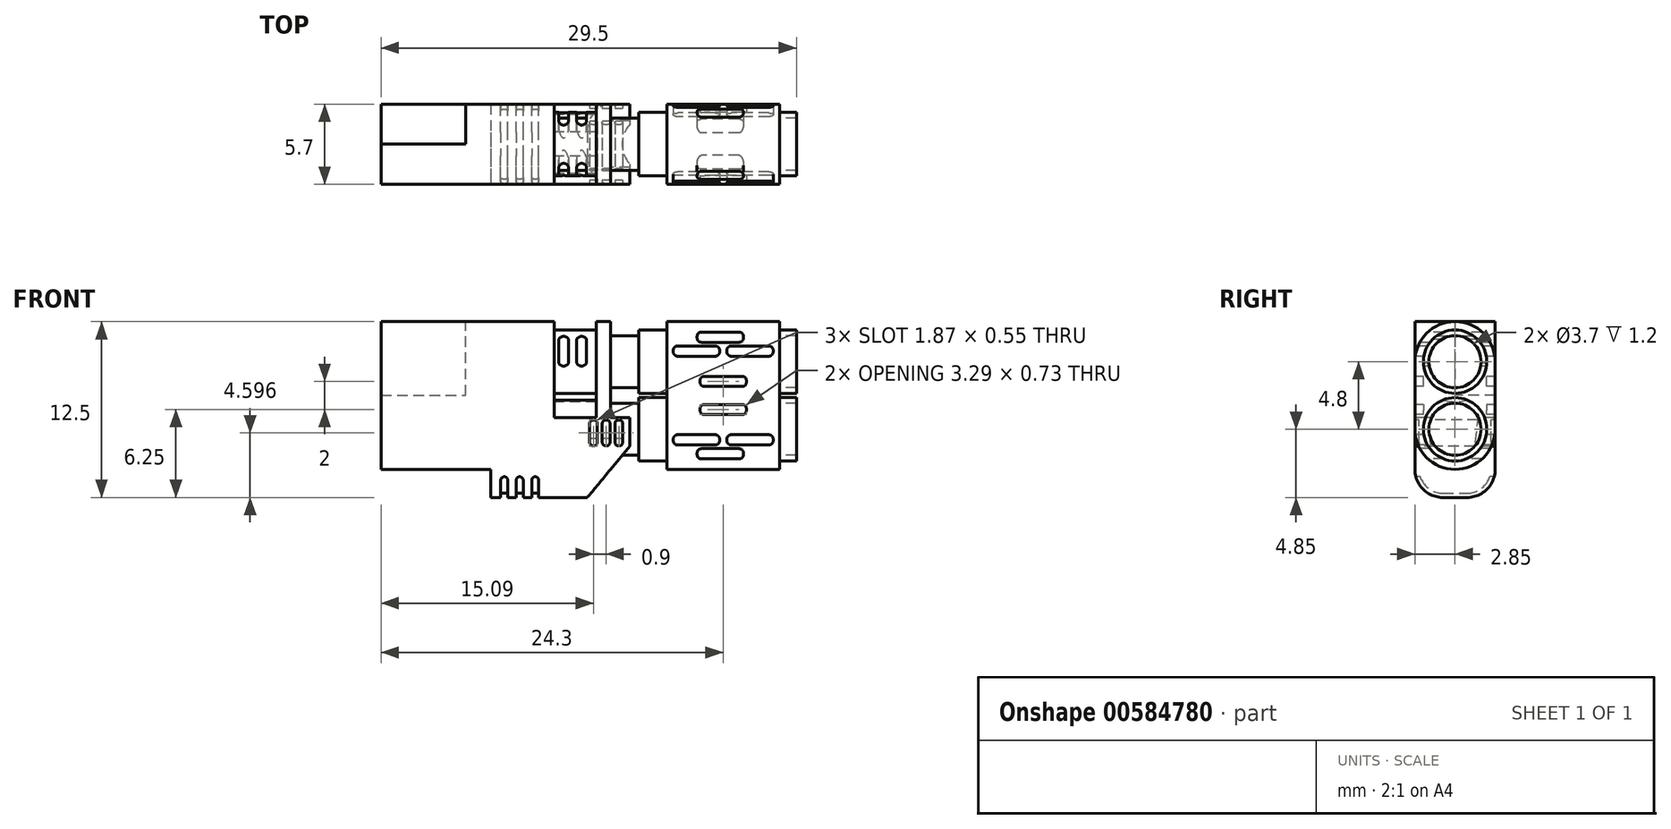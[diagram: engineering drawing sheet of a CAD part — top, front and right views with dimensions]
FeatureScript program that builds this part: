
annotation { "Feature Type Name" : "Feature", "Feature Type Description" : "" }
export const myFeature = defineFeature(function(context is Context, id is Id, definition is map)
    precondition{}
    {
        {
            var Q0;
            Q0=qCreatedBy(makeId("Front.planeOp"),FACE);
            var sketch = newSketch(context, id + "F0", { "sketchPlane" : qUnion([Q0])});
            skLineSegment(sketch, "E0.bottom", {"start": v(-20.5, 0) * mm, "end": v(-8.2, 0) * mm});
            skLineSegment(sketch, "E0.top", {"start": v(-20.5, 10.5) * mm, "end": v(-8.2, 10.5) * mm});
            skLineSegment(sketch, "E0.left", {"start": v(-20.5, 0) * mm, "end": v(-20.5, 10.5) * mm});
            skLineSegment(sketch, "E0.right", {"start": v(-8.2, 0) * mm, "end": v(-8.2, 10.5) * mm});
            skLineSegment(sketch, "E1", {"start": v(-20.5, 5.25) * mm, "end": v(-14.5, 5.25) * mm});
            skPoint(sketch, "E1.endSnap0", {"position": v(-20.5, 5.25) * mm});
            skLineSegment(sketch, "E2", {"start": v(-14.5, 5.25) * mm, "end": v(-14.5, 10.5) * mm});
            skLineSegment(sketch, "E3", {"start": v(-12.7, 2.94) * mm, "end": v(-12.7, 0) * mm, "construction": true});
            skSolve(sketch);
        }
        {
            var Q0;
            {var subQ1=sQuery(id+"F0.wireOp",EDGE,"E0.bottom");Q0=makeQuery(id+"F0.imprint","IMPRINT",FACE,{"disambiguationData":[TD([[makeQuery(id+"F0.imprint","IMPRINT",EDGE,{"derivedFrom":subQ1}),1.0]])]});}
            extrude(context, id + "F1", {"entities" : qUnion([Q0]), "oppositeDirection" : true, "depth" : 5.7 * mm, "offsetDistance" : 25 * mm});
        }
        {
            var Q0;
            {var subQ4=sQuery(id+"F0.wireOp",EDGE,"E1");Q0=makeQuery(id+"F0.imprint","IMPRINT",FACE,{"disambiguationData":[TD([[makeQuery(id+"F0.imprint","IMPRINT",EDGE,{"derivedFrom":subQ4}),1.0]])]});}
            extrude(context, id + "F2", {"entities" : qUnion([Q0]), "operationType" : NewBodyOperationType.ADD, "oppositeDirection" : true, "depth" : 2.87 * mm, "offsetDistance" : 25 * mm});
        }
        {
            var Q0;
            Q0=makeQuery(id+"F1.opExtrude","SWEPT_FACE",FACE,{"disambiguationData":[OSD([sQuery(id+"F0.wireOp",EDGE,"E0.right")])]});
            var sketch = newSketch(context, id + "F3", { "sketchPlane" : qUnion([Q0])});
            skArc(sketch, "E4", {"start": v(5.7, 7.65) * mm, "mid": v(2.85, 10.5) * mm, "end": v(0, 7.65) * mm});
            skArc(sketch, "E5", {"start": v(0, 2.85) * mm, "mid": v(2.85, 0) * mm, "end": v(5.7, 2.85) * mm});
            skPoint(sketch, "E5.centerSnap0", {"position": v(2.85, 10.5) * mm});
            skLineSegment(sketch, "E6", {"start": v(2.85, 10.5) * mm, "end": v(2.85, 0) * mm, "construction": true});
            skPoint(sketch, "E7", {"position": v(0, 7.65) * mm});
            skPoint(sketch, "E8", {"position": v(5.7, 7.65) * mm});
            skPoint(sketch, "E9", {"position": v(5.7, 2.85) * mm});
            skPoint(sketch, "E10", {"position": v(0, 2.85) * mm});
            skLineSegment(sketch, "E11", {"start": v(0, 7.65) * mm, "end": v(0, 2.85) * mm});
            skLineSegment(sketch, "E12", {"start": v(5.7, 7.65) * mm, "end": v(5.7, 2.85) * mm});
            skCircle(sketch, "E13", {"center": v(2.85, 7.65) * mm, "radius": 2.25 * mm});
            skCircle(sketch, "E14", {"center": v(2.85, 2.85) * mm, "radius": 2.25 * mm});
            skCircle(sketch, "E15", {"center": v(2.85, 2.85) * mm, "radius": 2.85 * mm});
            skCircle(sketch, "E16", {"center": v(2.85, 7.65) * mm, "radius": 2.85 * mm});
            skCircle(sketch, "E17", {"center": v(2.85, 7.65) * mm, "radius": 1.85 * mm});
            skCircle(sketch, "E18", {"center": v(2.85, 2.85) * mm, "radius": 1.85 * mm});
            skSolve(sketch);
        }
        {
            var Q0;
            Q0=makeQuery(id+"F3.imprint","IMPRINT",FACE,{"disambiguationData":[TD([[makeQuery(id+"F3.imprint","IMPRINT",EDGE,{"derivedFrom":sQuery(id+"F3.wireOp",EDGE,"E17")}),-1.0]])]});
            var Q1;
            Q1=makeQuery(id+"F3.imprint","IMPRINT",FACE,{"disambiguationData":[TD([[makeQuery(id+"F3.imprint","IMPRINT",EDGE,{"derivedFrom":sQuery(id+"F3.wireOp",EDGE,"E17")}),1.0]])]});
            var Q2;
            Q2=makeQuery(id+"F3.imprint","IMPRINT",FACE,{"disambiguationData":[TD([[makeQuery(id+"F3.imprint","IMPRINT",EDGE,{"derivedFrom":sQuery(id+"F3.wireOp",EDGE,"E18")}),-1.0]])]});
            var Q3;
            Q3=makeQuery(id+"F3.imprint","IMPRINT",FACE,{"disambiguationData":[TD([[makeQuery(id+"F3.imprint","IMPRINT",EDGE,{"derivedFrom":sQuery(id+"F3.wireOp",EDGE,"E18")}),1.0]])]});
            var Q4;
            {var subQ0=sQuery(id+"F3.wireOp",EDGE,"E16");var subQ1=sQuery(id+"F3.wireOp",EDGE,"E14");var subQ2=makeQuery(id+"F3.imprint","INTERSECT",VERTEX,{"disambiguationData":[OD(0.0)],"derivedFrom":[subQ1,subQ0]});Q4=makeQuery(id+"F3.imprint","IMPRINT",FACE,{"disambiguationData":[TD([[makeQuery(id+"F3.imprint","IMPRINT",EDGE,{"disambiguationData":[TD([[subQ2,1.0]])],"derivedFrom":subQ1}),1.0]])]});}
            var Q5;
            {var subQ0=sQuery(id+"F3.wireOp",EDGE,"E15");var subQ1=sQuery(id+"F3.wireOp",EDGE,"E13");var subQ2=makeQuery(id+"F3.imprint","INTERSECT",VERTEX,{"disambiguationData":[OD(0.0)],"derivedFrom":[subQ1,subQ0]});Q5=makeQuery(id+"F3.imprint","IMPRINT",FACE,{"disambiguationData":[TD([[makeQuery(id+"F3.imprint","IMPRINT",EDGE,{"disambiguationData":[TD([[subQ2,1.0]])],"derivedFrom":subQ1}),1.0]])]});}
            extrude(context, id + "F4", {"entities" : qUnion([Q0, Q1, Q2, Q3, Q4, Q5]), "operationType" : NewBodyOperationType.ADD, "depth" : 3 * mm, "offsetDistance" : 25 * mm});
        }
        {
            var Q0;
            Q0=makeQuery(id+"F4.opExtrude","CAP_FACE",FACE,{"disambiguationData":[OSD([sQuery(id+"F3.wireOp",EDGE,"E13")])],"isStart":false});
            var sketch = newSketch(context, id + "F5", { "sketchPlane" : qUnion([Q0])});
            skArc(sketch, "E19.0", {"start": v(5.7, 7.65) * mm, "mid": v(2.85, 10.5) * mm, "end": v(0, 7.65) * mm});
            skArc(sketch, "E19.1", {"start": v(0, 2.85) * mm, "mid": v(2.85, 0) * mm, "end": v(5.7, 2.85) * mm});
            skLineSegment(sketch, "E19.2", {"start": v(0, 7.65) * mm, "end": v(0, 2.85) * mm});
            skLineSegment(sketch, "E19.3", {"start": v(5.7, 7.65) * mm, "end": v(5.7, 2.85) * mm});
            skSolve(sketch);
        }
        {
            var Q0;
            Q0 = qSketchRegion(id + "F5", true);
            extrude(context, id + "F6", {"entities" : qUnion([Q0]), "operationType" : NewBodyOperationType.ADD, "depth" : 1 * mm, "offsetDistance" : 25 * mm});
        }
        {
            var Q0;
            Q0=makeQuery(id+"F6.opExtrude","CAP_FACE",FACE,{"disambiguationData":[OSD([sQuery(id+"F5.wireOp",EDGE,"E19.0"),sQuery(id+"F5.wireOp",EDGE,"E19.1"),sQuery(id+"F5.wireOp",EDGE,"E19.2"),sQuery(id+"F5.wireOp",EDGE,"E19.3")])],"isStart":false});
            var sketch = newSketch(context, id + "F7", { "sketchPlane" : qUnion([Q0])});
            skCircle(sketch, "E20.0", {"center": v(2.85, 7.65) * mm, "radius": 1.85 * mm});
            skCircle(sketch, "E20.1", {"center": v(2.85, 2.85) * mm, "radius": 1.85 * mm});
            skSolve(sketch);
        }
        {
            var Q0;
            Q0=makeQuery(id+"F7.imprint","IMPRINT",FACE,{"disambiguationData":[TD([[makeQuery(id+"F7.imprint","IMPRINT",EDGE,{"derivedFrom":sQuery(id+"F7.wireOp",EDGE,"E20.0")}),1.0]])]});
            var Q1;
            Q1=makeQuery(id+"F7.imprint","IMPRINT",FACE,{"disambiguationData":[TD([[makeQuery(id+"F7.imprint","IMPRINT",EDGE,{"derivedFrom":sQuery(id+"F7.wireOp",EDGE,"E20.1")}),1.0]])]});
            extrude(context, id + "F8", {"entities" : qUnion([Q0, Q1]), "operationType" : NewBodyOperationType.ADD, "depth" : 2 * mm, "offsetDistance" : 25 * mm});
        }
        {
            var Q0;
            Q0=makeQuery(id+"F8.opExtrude","CAP_FACE",FACE,{"disambiguationData":[OSD([sQuery(id+"F7.wireOp",EDGE,"E20.0")])],"isStart":false});
            var sketch = newSketch(context, id + "F9", { "sketchPlane" : qUnion([Q0])});
            skCircle(sketch, "E21.0", {"center": v(2.85, 7.65) * mm, "radius": 2.25 * mm});
            skCircle(sketch, "E21.1", {"center": v(2.85, 2.85) * mm, "radius": 2.25 * mm});
            skSolve(sketch);
        }
        {
            var Q0;
            Q0=makeQuery(id+"F9.imprint","IMPRINT",FACE,{"disambiguationData":[TD([[makeQuery(id+"F9.imprint","IMPRINT",EDGE,{"derivedFrom":sQuery(id+"F9.wireOp",EDGE,"E21.0")}),1.0]])]});
            var Q1;
            Q1=makeQuery(id+"F9.imprint","IMPRINT",FACE,{"disambiguationData":[TD([[makeQuery(id+"F9.imprint","IMPRINT",EDGE,{"derivedFrom":makeQuery(id+"F8.opExtrude","CAP_EDGE",EDGE,{"disambiguationData":[OSD([sQuery(id+"F7.wireOp",EDGE,"E20.0")])],"isStart":false})}),1.0]])]});
            var Q2;
            Q2=makeQuery(id+"F9.imprint","IMPRINT",FACE,{"disambiguationData":[TD([[makeQuery(id+"F9.imprint","IMPRINT",EDGE,{"derivedFrom":sQuery(id+"F9.wireOp",EDGE,"E21.1")}),1.0]])]});
            extrude(context, id + "F10", {"entities" : qUnion([Q0, Q1, Q2]), "operationType" : NewBodyOperationType.ADD, "depth" : 2 * mm, "offsetDistance" : 25 * mm});
        }
        {
            var Q0;
            Q0=makeQuery(id+"F10.opExtrude","CAP_FACE",FACE,{"disambiguationData":[OSD([sQuery(id+"F9.wireOp",EDGE,"E21.0")])],"isStart":false});
            var sketch = newSketch(context, id + "F11", { "sketchPlane" : qUnion([Q0])});
            skLineSegment(sketch, "E22.0.0", {"start": v(0, 7.65) * mm, "end": v(0, 2.85) * mm});
            skArc(sketch, "E22.0.1", {"start": v(0, 2.85) * mm, "mid": v(2.85, 0) * mm, "end": v(5.7, 2.85) * mm});
            skLineSegment(sketch, "E22.0.2", {"start": v(5.7, 2.85) * mm, "end": v(5.7, 7.65) * mm});
            skArc(sketch, "E22.0.3", {"start": v(5.7, 7.65) * mm, "mid": v(2.85, 10.5) * mm, "end": v(0, 7.65) * mm});
            skSolve(sketch);
        }
        {
            var Q0;
            Q0=makeQuery(id+"F11.imprint","IMPRINT",FACE,{"disambiguationData":[TD([[makeQuery(id+"F11.imprint","IMPRINT",EDGE,{"derivedFrom":makeQuery(id+"F10.opExtrude","CAP_EDGE",EDGE,{"disambiguationData":[OSD([sQuery(id+"F9.wireOp",EDGE,"E21.0")])],"isStart":false})}),1.0]])]});
            var Q1;
            Q1=makeQuery(id+"F11.imprint","IMPRINT",FACE,{"disambiguationData":[TD([[makeQuery(id+"F11.imprint","IMPRINT",EDGE,{"derivedFrom":sQuery(id+"F11.wireOp",EDGE,"E22.0.0")}),1.0]])]});
            extrude(context, id + "F12", {"entities" : qUnion([Q0, Q1]), "operationType" : NewBodyOperationType.ADD, "depth" : 8 * mm, "offsetDistance" : 25 * mm});
        }
        {
            var Q0;
            Q0=makeQuery(id+"F12.opExtrude","CAP_FACE",FACE,{"disambiguationData":[OSD([sQuery(id+"F11.wireOp",EDGE,"E22.0.0"),sQuery(id+"F11.wireOp",EDGE,"E22.0.1"),sQuery(id+"F11.wireOp",EDGE,"E22.0.2"),sQuery(id+"F11.wireOp",EDGE,"E22.0.3")])],"isStart":false});
            var sketch = newSketch(context, id + "F13", { "sketchPlane" : qUnion([Q0])});
            skCircle(sketch, "E23.0", {"center": v(2.85, 7.65) * mm, "radius": 2.25 * mm});
            skCircle(sketch, "E23.1", {"center": v(2.85, 7.65) * mm, "radius": 1.85 * mm});
            skCircle(sketch, "E23.2", {"center": v(2.85, 2.85) * mm, "radius": 2.25 * mm});
            skCircle(sketch, "E23.3", {"center": v(2.85, 2.85) * mm, "radius": 1.85 * mm});
            skSolve(sketch);
        }
        {
            var Q0;
            Q0=makeQuery(id+"F13.imprint","IMPRINT",FACE,{"disambiguationData":[TD([[makeQuery(id+"F13.imprint","IMPRINT",EDGE,{"derivedFrom":sQuery(id+"F13.wireOp",EDGE,"E23.0")}),1.0]])]});
            var Q1;
            Q1=makeQuery(id+"F13.imprint","IMPRINT",FACE,{"disambiguationData":[TD([[makeQuery(id+"F13.imprint","IMPRINT",EDGE,{"derivedFrom":sQuery(id+"F13.wireOp",EDGE,"E23.2")}),1.0]])]});
            extrude(context, id + "F14", {"entities" : qUnion([Q0, Q1]), "operationType" : NewBodyOperationType.ADD, "depth" : 1.2 * mm, "offsetDistance" : 25 * mm});
        }
        {
            var Q0;
            {var subQ1=sQuery(id+"F0.wireOp",EDGE,"E0.bottom");Q0=makeQuery(id+"F0.imprint","IMPRINT",FACE,{"disambiguationData":[TD([[makeQuery(id+"F0.imprint","IMPRINT",EDGE,{"derivedFrom":subQ1}),1.0]])]});}
            var sketch = newSketch(context, id + "F15", { "sketchPlane" : qUnion([Q0])});
            skLineSegment(sketch, "E24", {"start": v(-7.53, 9.45) * mm, "end": v(-7.53, 7.34) * mm});
            skLineSegment(sketch, "E25.bottom", {"start": v(-7.18, 9.23) * mm, "end": v(-7.88, 9.23) * mm});
            skLineSegment(sketch, "E25.top", {"start": v(-7.18, 7.55) * mm, "end": v(-7.88, 7.55) * mm});
            skLineSegment(sketch, "E25.left", {"start": v(-7.18, 9.23) * mm, "end": v(-7.18, 7.55) * mm});
            skLineSegment(sketch, "E25.right", {"start": v(-7.88, 9.23) * mm, "end": v(-7.88, 7.55) * mm});
            skPoint(sketch, "E25.middle", {"position": v(-7.53, 8.4) * mm});
            skArc(sketch, "E26", {"start": v(-7.18, 9.23) * mm, "mid": v(-7.53, 9.45) * mm, "end": v(-7.88, 9.23) * mm});
            skArc(sketch, "E27", {"start": v(-7.88, 7.55) * mm, "mid": v(-7.53, 7.34) * mm, "end": v(-7.18, 7.55) * mm});
            skLineSegment(sketch, "E28", {"start": v(-7.88, 9.23) * mm, "end": v(-5.81, 9.23) * mm, "construction": true});
            skLineSegment(sketch, "E29", {"start": v(-7.53, 8.4) * mm, "end": v(-5.83, 8.4) * mm, "construction": true});
            skLineSegment(sketch, "E30", {"start": v(-6.9, 9.77) * mm, "end": v(-6.9, 7.35) * mm, "construction": true});
            skLineSegment(sketch, "E31.MirrorCS", {"start": v(-6.6, 9.23) * mm, "end": v(-6.6, 7.55) * mm});
            skArc(sketch, "E32.MirrorCS", {"start": v(-6.6, 9.23) * mm, "mid": v(-6.25, 9.45) * mm, "end": v(-5.9, 9.23) * mm});
            skLineSegment(sketch, "E33.MirrorCS", {"start": v(-5.9, 9.23) * mm, "end": v(-5.9, 7.55) * mm});
            skArc(sketch, "E34.MirrorCS", {"start": v(-5.9, 7.55) * mm, "mid": v(-6.25, 7.34) * mm, "end": v(-6.6, 7.55) * mm});
            skSolve(sketch);
        }
        {
            var Q0;
            {var subQ0=sQuery(id+"F15.wireOp",EDGE,"E26");var subQ1=sQuery(id+"F15.wireOp",EDGE,"E24");var subQ2=makeQuery(id+"F15.imprint","INTERSECT",VERTEX,{"derivedFrom":[subQ1,subQ0]});Q0=makeQuery(id+"F15.imprint","IMPRINT",FACE,{"disambiguationData":[TD([[makeQuery(id+"F15.imprint","IMPRINT",EDGE,{"disambiguationData":[TD([[subQ2,-1.0]])],"derivedFrom":subQ1}),-1.0]])]});}
            var Q1;
            {var subQ0=sQuery(id+"F15.wireOp",EDGE,"E26");var subQ1=sQuery(id+"F15.wireOp",EDGE,"E24");var subQ2=makeQuery(id+"F15.imprint","INTERSECT",VERTEX,{"derivedFrom":[subQ1,subQ0]});Q1=makeQuery(id+"F15.imprint","IMPRINT",FACE,{"disambiguationData":[TD([[makeQuery(id+"F15.imprint","IMPRINT",EDGE,{"disambiguationData":[TD([[subQ2,-1.0]])],"derivedFrom":subQ1}),1.0]])]});}
            var Q2;
            {var subQ5=sQuery(id+"F15.wireOp",EDGE,"E25.left");Q2=makeQuery(id+"F15.imprint","IMPRINT",FACE,{"disambiguationData":[TD([[makeQuery(id+"F15.imprint","IMPRINT",EDGE,{"derivedFrom":subQ5}),-1.0]])]});}
            var Q3;
            {var subQ5=sQuery(id+"F15.wireOp",EDGE,"E25.right");Q3=makeQuery(id+"F15.imprint","IMPRINT",FACE,{"disambiguationData":[TD([[makeQuery(id+"F15.imprint","IMPRINT",EDGE,{"derivedFrom":subQ5}),1.0]])]});}
            var Q4;
            {var subQ0=sQuery(id+"F15.wireOp",EDGE,"E27");var subQ1=sQuery(id+"F15.wireOp",EDGE,"E24");var subQ2=makeQuery(id+"F15.imprint","INTERSECT",VERTEX,{"derivedFrom":[subQ1,subQ0]});Q4=makeQuery(id+"F15.imprint","IMPRINT",FACE,{"disambiguationData":[TD([[makeQuery(id+"F15.imprint","IMPRINT",EDGE,{"disambiguationData":[TD([[subQ2,1.0]])],"derivedFrom":subQ1}),-1.0]])]});}
            var Q5;
            {var subQ0=sQuery(id+"F15.wireOp",EDGE,"E27");var subQ1=sQuery(id+"F15.wireOp",EDGE,"E24");var subQ2=makeQuery(id+"F15.imprint","INTERSECT",VERTEX,{"derivedFrom":[subQ1,subQ0]});Q5=makeQuery(id+"F15.imprint","IMPRINT",FACE,{"disambiguationData":[TD([[makeQuery(id+"F15.imprint","IMPRINT",EDGE,{"disambiguationData":[TD([[subQ2,1.0]])],"derivedFrom":subQ1}),1.0]])]});}
            extrude(context, id + "F16", {"entities" : qUnion([Q0, Q1, Q2, Q3, Q4, Q5]), "operationType" : NewBodyOperationType.REMOVE, "oppositeDirection" : true, "depth" : 6 * mm, "offsetDistance" : 25 * mm});
        }
        {
            var Q0;
            Q0=makeQuery(id+"F15.imprint","IMPRINT",FACE,{"disambiguationData":[TD([[makeQuery(id+"F15.imprint","IMPRINT",EDGE,{"derivedFrom":sQuery(id+"F15.wireOp",EDGE,"E31.MirrorCS")}),1.0]])]});
            extrude(context, id + "F17", {"entities" : qUnion([Q0]), "operationType" : NewBodyOperationType.REMOVE, "oppositeDirection" : true, "depth" : 6 * mm, "offsetDistance" : 25 * mm});
        }
        {
            var Q0;
            Q0=makeQuery(id+"F3.imprint","IMPRINT",FACE,{"disambiguationData":[TD([[makeQuery(id+"F3.imprint","IMPRINT",EDGE,{"derivedFrom":sQuery(id+"F3.wireOp",EDGE,"E17")}),1.0]])]});
            extrude(context, id + "F18", {"entities" : qUnion([Q0]), "operationType" : NewBodyOperationType.ADD, "depth" : 5 * mm, "offsetDistance" : 25 * mm});
        }
        {
            var Q0;
            Q0=makeQuery(id+"F12.opExtrude","SWEPT_FACE",FACE,{"disambiguationData":[OSD([sQuery(id+"F11.wireOp",EDGE,"E22.0.0")])]});
            var sketch = newSketch(context, id + "F19", { "sketchPlane" : qUnion([Q0])});
            skLineSegment(sketch, "E35", {"start": v(-0.2, 5.25) * mm, "end": v(7.8, 5.25) * mm, "construction": true});
            skLineSegment(sketch, "E36", {"start": v(3.8, 5.25) * mm, "end": v(3.8, 10.5) * mm, "construction": true});
            skLineSegment(sketch, "E37.bottom", {"start": v(5.14, 5.89) * mm, "end": v(2.46, 5.89) * mm});
            skLineSegment(sketch, "E37.top", {"start": v(5.14, 6.61) * mm, "end": v(2.46, 6.61) * mm});
            skLineSegment(sketch, "E37.left", {"start": v(5.44, 6.19) * mm, "end": v(5.44, 6.31) * mm});
            skLineSegment(sketch, "E37.right", {"start": v(2.16, 6.19) * mm, "end": v(2.16, 6.31) * mm});
            skPoint(sketch, "E37.middle", {"position": v(3.8, 6.25) * mm});
            skPoint(sketch, "E38.visualSharp", {"position": v(2.16, 6.61) * mm});
            skArc(sketch, "E38.filletArc", {"start": v(2.46, 6.61) * mm, "mid": v(2.24, 6.53) * mm, "end": v(2.16, 6.31) * mm});
            skPoint(sketch, "E39.visualSharp", {"position": v(2.16, 5.89) * mm});
            skArc(sketch, "E39.filletArc", {"start": v(2.16, 6.19) * mm, "mid": v(2.24, 5.97) * mm, "end": v(2.46, 5.89) * mm});
            skPoint(sketch, "E40.visualSharp", {"position": v(5.44, 6.61) * mm});
            skArc(sketch, "E40.filletArc", {"start": v(5.44, 6.31) * mm, "mid": v(5.36, 6.53) * mm, "end": v(5.14, 6.61) * mm});
            skPoint(sketch, "E41.visualSharp", {"position": v(5.44, 5.89) * mm});
            skArc(sketch, "E41.filletArc", {"start": v(5.14, 5.89) * mm, "mid": v(5.36, 5.97) * mm, "end": v(5.44, 6.19) * mm});
            skLineSegment(sketch, "E42.bottom", {"start": v(4.93, 9.03) * mm, "end": v(2.25, 9.03) * mm});
            skLineSegment(sketch, "E42.top", {"start": v(4.93, 9.75) * mm, "end": v(2.25, 9.75) * mm});
            skLineSegment(sketch, "E42.left", {"start": v(5.23, 9.33) * mm, "end": v(5.23, 9.45) * mm});
            skLineSegment(sketch, "E42.right", {"start": v(1.95, 9.33) * mm, "end": v(1.95, 9.45) * mm});
            skPoint(sketch, "E42.middle", {"position": v(3.6, 9.4) * mm});
            skPoint(sketch, "E43.visualSharp", {"position": v(1.95, 9.75) * mm});
            skArc(sketch, "E43.filletArc", {"start": v(2.25, 9.75) * mm, "mid": v(2.03, 9.67) * mm, "end": v(1.95, 9.45) * mm});
            skPoint(sketch, "E44.visualSharp", {"position": v(1.95, 9.03) * mm});
            skArc(sketch, "E44.filletArc", {"start": v(1.95, 9.33) * mm, "mid": v(2.03, 9.12) * mm, "end": v(2.25, 9.03) * mm});
            skPoint(sketch, "E45.visualSharp", {"position": v(5.23, 9.75) * mm});
            skArc(sketch, "E45.filletArc", {"start": v(5.23, 9.45) * mm, "mid": v(5.15, 9.67) * mm, "end": v(4.93, 9.75) * mm});
            skPoint(sketch, "E46.visualSharp", {"position": v(5.23, 9.03) * mm});
            skArc(sketch, "E46.filletArc", {"start": v(4.93, 9.03) * mm, "mid": v(5.15, 9.12) * mm, "end": v(5.23, 9.33) * mm});
            skLineSegment(sketch, "E47.bottom", {"start": v(3.24, 8.04) * mm, "end": v(0.55, 8.04) * mm});
            skLineSegment(sketch, "E47.top", {"start": v(3.24, 8.77) * mm, "end": v(0.55, 8.77) * mm});
            skLineSegment(sketch, "E47.left", {"start": v(3.54, 8.34) * mm, "end": v(3.54, 8.47) * mm});
            skLineSegment(sketch, "E47.right", {"start": v(0.25, 8.34) * mm, "end": v(0.25, 8.47) * mm});
            skPoint(sketch, "E47.middle", {"position": v(1.9, 8.4) * mm});
            skPoint(sketch, "E48.visualSharp", {"position": v(0.25, 8.77) * mm});
            skArc(sketch, "E48.filletArc", {"start": v(0.55, 8.77) * mm, "mid": v(0.34, 8.68) * mm, "end": v(0.25, 8.47) * mm});
            skPoint(sketch, "E49.visualSharp", {"position": v(0.25, 8.04) * mm});
            skArc(sketch, "E49.filletArc", {"start": v(0.25, 8.34) * mm, "mid": v(0.34, 8.13) * mm, "end": v(0.55, 8.04) * mm});
            skPoint(sketch, "E50.visualSharp", {"position": v(3.54, 8.77) * mm});
            skArc(sketch, "E50.filletArc", {"start": v(3.54, 8.47) * mm, "mid": v(3.45, 8.68) * mm, "end": v(3.24, 8.77) * mm});
            skPoint(sketch, "E51.visualSharp", {"position": v(3.54, 8.04) * mm});
            skArc(sketch, "E51.filletArc", {"start": v(3.24, 8.04) * mm, "mid": v(3.45, 8.13) * mm, "end": v(3.54, 8.34) * mm});
            skLineSegment(sketch, "E52.MirrorCS", {"start": v(4.06, 8.34) * mm, "end": v(4.06, 8.47) * mm});
            skLineSegment(sketch, "E53.MirrorCS", {"start": v(7.35, 8.34) * mm, "end": v(7.35, 8.47) * mm});
            skArc(sketch, "E54.MirrorCS", {"start": v(7.35, 8.34) * mm, "mid": v(7.26, 8.13) * mm, "end": v(7.05, 8.04) * mm});
            skArc(sketch, "E55.MirrorCS", {"start": v(4.06, 8.47) * mm, "mid": v(4.15, 8.68) * mm, "end": v(4.36, 8.77) * mm});
            skArc(sketch, "E56.MirrorCS", {"start": v(4.36, 8.04) * mm, "mid": v(4.15, 8.13) * mm, "end": v(4.06, 8.34) * mm});
            skArc(sketch, "E57.MirrorCS", {"start": v(7.05, 8.77) * mm, "mid": v(7.26, 8.68) * mm, "end": v(7.35, 8.47) * mm});
            skPoint(sketch, "E58.MirrorP", {"position": v(7.35, 8.77) * mm});
            skPoint(sketch, "E59.MirrorP", {"position": v(4.06, 8.04) * mm});
            skPoint(sketch, "E60.MirrorP", {"position": v(4.06, 8.77) * mm});
            skLineSegment(sketch, "E61.MirrorCS", {"start": v(4.36, 8.04) * mm, "end": v(7.05, 8.04) * mm});
            skLineSegment(sketch, "E62.MirrorCS", {"start": v(4.36, 8.77) * mm, "end": v(7.05, 8.77) * mm});
            skPoint(sketch, "E63.MirrorP", {"position": v(7.35, 8.04) * mm});
            skPoint(sketch, "E64.MirrorP", {"position": v(5.7, 8.4) * mm});
            skLineSegment(sketch, "E65.MirrorCS", {"start": v(7.35, 2.16) * mm, "end": v(7.35, 2.03) * mm});
            skLineSegment(sketch, "E66.MirrorCS", {"start": v(1.95, 1.17) * mm, "end": v(1.95, 1.05) * mm});
            skLineSegment(sketch, "E67.MirrorCS", {"start": v(3.54, 2.16) * mm, "end": v(3.54, 2.03) * mm});
            skLineSegment(sketch, "E68.MirrorCS", {"start": v(5.44, 4.31) * mm, "end": v(5.44, 4.19) * mm});
            skLineSegment(sketch, "E69.MirrorCS", {"start": v(2.16, 4.31) * mm, "end": v(2.16, 4.19) * mm});
            skLineSegment(sketch, "E70.MirrorCS", {"start": v(0.25, 2.16) * mm, "end": v(0.25, 2.03) * mm});
            skLineSegment(sketch, "E71.MirrorCS", {"start": v(4.06, 2.16) * mm, "end": v(4.06, 2.03) * mm});
            skLineSegment(sketch, "E72.MirrorCS", {"start": v(5.23, 1.17) * mm, "end": v(5.23, 1.05) * mm});
            skArc(sketch, "E73.MirrorCS", {"start": v(1.95, 1.17) * mm, "mid": v(2.03, 1.38) * mm, "end": v(2.25, 1.47) * mm});
            skArc(sketch, "E74.MirrorCS", {"start": v(2.25, 0.75) * mm, "mid": v(2.03, 0.83) * mm, "end": v(1.95, 1.05) * mm});
            skArc(sketch, "E75.MirrorCS", {"start": v(5.23, 1.05) * mm, "mid": v(5.15, 0.83) * mm, "end": v(4.93, 0.75) * mm});
            skArc(sketch, "E76.MirrorCS", {"start": v(0.25, 2.16) * mm, "mid": v(0.34, 2.37) * mm, "end": v(0.55, 2.46) * mm});
            skArc(sketch, "E77.MirrorCS", {"start": v(4.06, 2.03) * mm, "mid": v(4.15, 1.82) * mm, "end": v(4.36, 1.73) * mm});
            skArc(sketch, "E78.MirrorCS", {"start": v(2.46, 3.89) * mm, "mid": v(2.24, 3.97) * mm, "end": v(2.16, 4.19) * mm});
            skArc(sketch, "E79.MirrorCS", {"start": v(4.36, 2.46) * mm, "mid": v(4.15, 2.37) * mm, "end": v(4.06, 2.16) * mm});
            skArc(sketch, "E80.MirrorCS", {"start": v(2.16, 4.31) * mm, "mid": v(2.24, 4.53) * mm, "end": v(2.46, 4.61) * mm});
            skArc(sketch, "E81.MirrorCS", {"start": v(5.44, 4.19) * mm, "mid": v(5.36, 3.97) * mm, "end": v(5.14, 3.89) * mm});
            skArc(sketch, "E82.MirrorCS", {"start": v(5.14, 4.61) * mm, "mid": v(5.36, 4.53) * mm, "end": v(5.44, 4.31) * mm});
            skArc(sketch, "E83.MirrorCS", {"start": v(3.24, 2.46) * mm, "mid": v(3.45, 2.37) * mm, "end": v(3.54, 2.16) * mm});
            skArc(sketch, "E84.MirrorCS", {"start": v(0.55, 1.73) * mm, "mid": v(0.34, 1.82) * mm, "end": v(0.25, 2.03) * mm});
            skArc(sketch, "E85.MirrorCS", {"start": v(7.05, 1.73) * mm, "mid": v(7.26, 1.82) * mm, "end": v(7.35, 2.03) * mm});
            skArc(sketch, "E86.MirrorCS", {"start": v(7.35, 2.16) * mm, "mid": v(7.26, 2.37) * mm, "end": v(7.05, 2.46) * mm});
            skArc(sketch, "E87.MirrorCS", {"start": v(4.93, 1.47) * mm, "mid": v(5.15, 1.38) * mm, "end": v(5.23, 1.17) * mm});
            skArc(sketch, "E88.MirrorCS", {"start": v(3.54, 2.03) * mm, "mid": v(3.45, 1.82) * mm, "end": v(3.24, 1.73) * mm});
            skPoint(sketch, "E89.MirrorP", {"position": v(5.7, 2.1) * mm});
            skLineSegment(sketch, "E90.MirrorCS", {"start": v(4.36, 2.46) * mm, "end": v(7.05, 2.46) * mm});
            skPoint(sketch, "E91.MirrorP", {"position": v(2.16, 4.61) * mm});
            skPoint(sketch, "E92.MirrorP", {"position": v(0.25, 1.73) * mm});
            skPoint(sketch, "E93.MirrorP", {"position": v(3.8, 4.25) * mm});
            skPoint(sketch, "E94.MirrorP", {"position": v(5.23, 1.47) * mm});
            skPoint(sketch, "E95.MirrorP", {"position": v(3.8, 1.1) * mm});
            skPoint(sketch, "E96.MirrorP", {"position": v(4.06, 2.46) * mm});
            skPoint(sketch, "E97.MirrorP", {"position": v(3.54, 2.46) * mm});
            skLineSegment(sketch, "E98.MirrorCS", {"start": v(5.14, 4.61) * mm, "end": v(2.46, 4.61) * mm});
            skLineSegment(sketch, "E99.MirrorCS", {"start": v(5.14, 3.89) * mm, "end": v(2.46, 3.89) * mm});
            skPoint(sketch, "E100.MirrorP", {"position": v(3.54, 1.73) * mm});
            skPoint(sketch, "E101.MirrorP", {"position": v(1.95, 1.47) * mm});
            skPoint(sketch, "E102.MirrorP", {"position": v(0.25, 2.46) * mm});
            skLineSegment(sketch, "E103.MirrorCS", {"start": v(3.24, 1.73) * mm, "end": v(0.55, 1.73) * mm});
            skPoint(sketch, "E104.MirrorP", {"position": v(1.9, 2.1) * mm});
            skPoint(sketch, "E105.MirrorP", {"position": v(7.35, 2.46) * mm});
            skPoint(sketch, "E106.MirrorP", {"position": v(7.35, 1.73) * mm});
            skLineSegment(sketch, "E107.MirrorCS", {"start": v(4.93, 1.47) * mm, "end": v(2.25, 1.47) * mm});
            skLineSegment(sketch, "E108.MirrorCS", {"start": v(4.93, 0.75) * mm, "end": v(2.25, 0.75) * mm});
            skLineSegment(sketch, "E109.MirrorCS", {"start": v(4.36, 1.73) * mm, "end": v(7.05, 1.73) * mm});
            skLineSegment(sketch, "E110.MirrorCS", {"start": v(3.24, 2.46) * mm, "end": v(0.55, 2.46) * mm});
            skPoint(sketch, "E111.MirrorP", {"position": v(4.06, 1.73) * mm});
            skPoint(sketch, "E112.MirrorP", {"position": v(1.95, 0.75) * mm});
            skPoint(sketch, "E113.MirrorP", {"position": v(5.44, 3.89) * mm});
            skPoint(sketch, "E114.MirrorP", {"position": v(2.16, 3.89) * mm});
            skPoint(sketch, "E115.MirrorP", {"position": v(5.23, 0.75) * mm});
            skPoint(sketch, "E116.MirrorP", {"position": v(5.44, 4.61) * mm});
            skLineSegment(sketch, "E117", {"start": v(0.25, 8.77) * mm, "end": v(0.25, 1.73) * mm, "construction": true});
            skLineSegment(sketch, "E118", {"start": v(7.35, 8.77) * mm, "end": v(7.35, 1.73) * mm, "construction": true});
            skPoint(sketch, "E119", {"position": v(0.25, 5.25) * mm});
            skPoint(sketch, "E120", {"position": v(7.35, 5.25) * mm});
            skLineSegment(sketch, "E121", {"start": v(3.54, 8.77) * mm, "end": v(3.54, 1.73) * mm, "construction": true});
            skLineSegment(sketch, "E122", {"start": v(4.06, 8.77) * mm, "end": v(4.06, 1.73) * mm, "construction": true});
            skLineSegment(sketch, "E123", {"start": v(0.25, 8.77) * mm, "end": v(7.35, 8.77) * mm, "construction": true});
            skLineSegment(sketch, "E124", {"start": v(0.25, 1.73) * mm, "end": v(7.35, 1.73) * mm, "construction": true});
            skLineSegment(sketch, "E125", {"start": v(0.25, 1.73) * mm, "end": v(2.16, 0.45) * mm, "construction": true});
            skLineSegment(sketch, "E126", {"start": v(5.23, 0.45) * mm, "end": v(7.35, 1.73) * mm, "construction": true});
            skPoint(sketch, "E127.0", {"position": v(-8.2, 5.25) * mm});
            skLineSegment(sketch, "E128", {"start": v(-8.2, 5.25) * mm, "end": v(0.25, 5.25) * mm, "construction": true});
            skLineSegment(sketch, "E129", {"start": v(1.95, 9.75) * mm, "end": v(1.95, 0.75) * mm, "construction": true});
            skLineSegment(sketch, "E130", {"start": v(5.23, 9.75) * mm, "end": v(5.23, 0.45) * mm, "construction": true});
            skLineSegment(sketch, "E131", {"start": v(3.8, 5.25) * mm, "end": v(3.8, 1.1) * mm, "construction": true});
            skSolve(sketch);
        }
        {
            var Q0;
            Q0=makeQuery(id+"F19.imprint","IMPRINT",FACE,{"disambiguationData":[TD([[makeQuery(id+"F19.imprint","IMPRINT",EDGE,{"derivedFrom":sQuery(id+"F19.wireOp",EDGE,"E47.bottom")}),-1.0]])]});
            var Q1;
            Q1=makeQuery(id+"F19.imprint","IMPRINT",FACE,{"disambiguationData":[TD([[makeQuery(id+"F19.imprint","IMPRINT",EDGE,{"derivedFrom":sQuery(id+"F19.wireOp",EDGE,"E42.bottom")}),-1.0]])]});
            var Q2;
            Q2=makeQuery(id+"F19.imprint","IMPRINT",FACE,{"disambiguationData":[TD([[makeQuery(id+"F19.imprint","IMPRINT",EDGE,{"derivedFrom":sQuery(id+"F19.wireOp",EDGE,"E52.MirrorCS")}),-1.0]])]});
            var Q3;
            Q3=makeQuery(id+"F19.imprint","IMPRINT",FACE,{"disambiguationData":[TD([[makeQuery(id+"F19.imprint","IMPRINT",EDGE,{"derivedFrom":sQuery(id+"F19.wireOp",EDGE,"E37.bottom")}),-1.0]])]});
            var Q4;
            Q4=makeQuery(id+"F19.imprint","IMPRINT",FACE,{"disambiguationData":[TD([[makeQuery(id+"F19.imprint","IMPRINT",EDGE,{"derivedFrom":sQuery(id+"F19.wireOp",EDGE,"E68.MirrorCS")}),-1.0]])]});
            var Q5;
            Q5=makeQuery(id+"F19.imprint","IMPRINT",FACE,{"disambiguationData":[TD([[makeQuery(id+"F19.imprint","IMPRINT",EDGE,{"derivedFrom":sQuery(id+"F19.wireOp",EDGE,"E65.MirrorCS")}),-1.0]])]});
            var Q6;
            Q6=makeQuery(id+"F19.imprint","IMPRINT",FACE,{"disambiguationData":[TD([[makeQuery(id+"F19.imprint","IMPRINT",EDGE,{"derivedFrom":sQuery(id+"F19.wireOp",EDGE,"E66.MirrorCS")}),1.0]])]});
            var Q7;
            Q7=makeQuery(id+"F19.imprint","IMPRINT",FACE,{"disambiguationData":[TD([[makeQuery(id+"F19.imprint","IMPRINT",EDGE,{"derivedFrom":sQuery(id+"F19.wireOp",EDGE,"E67.MirrorCS")}),-1.0]])]});
            extrude(context, id + "F20", {"entities" : qUnion([Q0, Q1, Q2, Q3, Q4, Q5, Q6, Q7]), "operationType" : NewBodyOperationType.REMOVE, "oppositeDirection" : true, "depth" : 8 * mm, "offsetDistance" : 25 * mm});
        }
        {
            var Q0;
            Q0=makeQuery(id+"F20.boolean.opBoolean","COPY",FACE,{"derivedFrom":makeQuery(id+"F20.opExtrude","SWEPT_FACE",FACE,{"disambiguationData":[OSD([sQuery(id+"F19.wireOp",EDGE,"E47.right")])]})});
            var sketch = newSketch(context, id + "F21", { "sketchPlane" : qUnion([Q0])});
            skCircle(sketch, "E132.0", {"center": v(2.85, 7.65) * mm, "radius": 2.25 * mm});
            skCircle(sketch, "E132.1", {"center": v(2.85, 2.85) * mm, "radius": 2.25 * mm});
            skPoint(sketch, "E133.0", {"position": v(0, 7.65) * mm});
            skPoint(sketch, "E133.1", {"position": v(5.7, 7.65) * mm});
            skPoint(sketch, "E134.0", {"position": v(0, 2.85) * mm});
            skPoint(sketch, "E134.1", {"position": v(5.7, 2.85) * mm});
            skLineSegment(sketch, "E135", {"start": v(0, 7.65) * mm, "end": v(5.7, 7.65) * mm, "construction": true});
            skLineSegment(sketch, "E136", {"start": v(0, 2.85) * mm, "end": v(5.7, 2.85) * mm, "construction": true});
            skLineSegment(sketch, "E137", {"start": v(0.6, 7.65) * mm, "end": v(0.6, 2.85) * mm});
            skLineSegment(sketch, "E138", {"start": v(5.1, 7.65) * mm, "end": v(5.1, 2.85) * mm});
            skSolve(sketch);
        }
        {
            var Q0;
            {var subQ0=sQuery(id+"F21.wireOp",EDGE,"E137");Q0=makeQuery(id+"F21.imprint","IMPRINT",FACE,{"disambiguationData":[TD([[makeQuery(id+"F21.imprint","IMPRINT",EDGE,{"derivedFrom":subQ0}),1.0]])]});}
            var Q1;
            {var subQ0=sQuery(id+"F21.wireOp",EDGE,"E132.0");var subQ4=makeQuery(id+"F21.imprint","INTERSECT",VERTEX,{"derivedFrom":[subQ0,sQuery(id+"F21.wireOp",EDGE,"E137")]});Q1=makeQuery(id+"F21.imprint","IMPRINT",FACE,{"disambiguationData":[TD([[makeQuery(id+"F21.imprint","IMPRINT",EDGE,{"disambiguationData":[TD([[subQ4,-1.0]])],"derivedFrom":subQ0}),1.0]])]});}
            var Q2;
            {var subQ0=sQuery(id+"F21.wireOp",EDGE,"E132.0");var subQ1=makeQuery(id+"F20.boolean.opBoolean","COPY",EDGE,{"derivedFrom":makeQuery(id+"F20.opExtrude","SWEPT_EDGE",EDGE,{"disambiguationData":[OSD([sQuery(id+"F19.wireOp",EDGE,"E47.right"),sQuery(id+"F19.wireOp",EDGE,"E48.filletArc")])]})});var subQ2=makeQuery(id+"F21.imprint","INTERSECT",VERTEX,{"disambiguationData":[OD(0.0)],"derivedFrom":[subQ1,subQ0]});Q2=makeQuery(id+"F21.imprint","IMPRINT",FACE,{"disambiguationData":[TD([[makeQuery(id+"F21.imprint","IMPRINT",EDGE,{"disambiguationData":[TD([[subQ2,-1.0]])],"derivedFrom":subQ0}),1.0]])]});}
            var Q3;
            {var subQ0=sQuery(id+"F21.wireOp",EDGE,"E132.0");var subQ1=sQuery(id+"F19.wireOp",EDGE,"E47.right");var subQ2=makeQuery(id+"F20.boolean.opBoolean","COPY",EDGE,{"derivedFrom":makeQuery(id+"F20.opExtrude","SWEPT_EDGE",EDGE,{"disambiguationData":[OSD([subQ1,sQuery(id+"F19.wireOp",EDGE,"E49.filletArc")])]})});var subQ3=makeQuery(id+"F21.imprint","INTERSECT",VERTEX,{"disambiguationData":[OD(0.0)],"derivedFrom":[subQ2,subQ0]});Q3=makeQuery(id+"F21.imprint","IMPRINT",FACE,{"disambiguationData":[TD([[makeQuery(id+"F21.imprint","IMPRINT",EDGE,{"disambiguationData":[TD([[subQ3,-1.0]])],"derivedFrom":subQ0}),1.0]])]});}
            var Q4;
            {var subQ0=sQuery(id+"F21.wireOp",EDGE,"E132.1");var subQ1=makeQuery(id+"F21.imprint","INTERSECT",VERTEX,{"derivedFrom":[subQ0,sQuery(id+"F21.wireOp",EDGE,"E137")]});Q4=makeQuery(id+"F21.imprint","IMPRINT",FACE,{"disambiguationData":[TD([[makeQuery(id+"F21.imprint","IMPRINT",EDGE,{"disambiguationData":[TD([[subQ1,1.0]])],"derivedFrom":subQ0}),1.0]])]});}
            extrude(context, id + "F22", {"entities" : qUnion([Q0, Q1, Q2, Q3, Q4]), "operationType" : NewBodyOperationType.ADD, "depth" : 7.25 * mm, "offsetDistance" : 25 * mm});
        }
        {
            var Q0;
            {var subQ2=sQuery(id+"F0.wireOp",EDGE,"E0.bottom");Q0=makeQuery(id+"F15.imprint","IMPRINT",FACE,{"disambiguationData":[TD([[makeQuery(id+"F15.imprint","IMPRINT",EDGE,{"derivedFrom":makeQuery(id+"F0.imprint","IMPRINT",EDGE,{"derivedFrom":subQ2})}),1.0]])]});}
            var sketch = newSketch(context, id + "F23", { "sketchPlane" : qUnion([Q0])});
            skLineSegment(sketch, "E139.0", {"start": v(-4.2, 7.65) * mm, "end": v(-4.2, 2.85) * mm});
            skLineSegment(sketch, "E139.1", {"start": v(-4.2, 7.65) * mm, "end": v(-5.2, 7.65) * mm});
            skLineSegment(sketch, "E139.2", {"start": v(-5.2, 7.65) * mm, "end": v(-5.2, 2.85) * mm});
            skLineSegment(sketch, "E139.4", {"start": v(-20.5, 0) * mm, "end": v(-8.2, 0) * mm});
            skLineSegment(sketch, "E139.5", {"start": v(-12.7, 2.94) * mm, "end": v(-12.7, 0) * mm});
            skLineSegment(sketch, "E140.0", {"start": v(-8.2, 7.65) * mm, "end": v(-8.2, 6.1) * mm});
            skPoint(sketch, "E141", {"position": v(-5.2, 5.25) * mm});
            skLineSegment(sketch, "E142", {"start": v(-12.7, 0) * mm, "end": v(-12.7, -2) * mm});
            skLineSegment(sketch, "E143", {"start": v(-12.7, -2) * mm, "end": v(-5.85, -2) * mm});
            skLineSegment(sketch, "E144", {"start": v(9.04, 8.5) * mm, "end": v(9.04, -4.33) * mm, "construction": true});
            skLineSegment(sketch, "E145", {"start": v(-2.83, 3.68) * mm, "end": v(-2.83, 1.66) * mm});
            skLineSegment(sketch, "E146", {"start": v(-2.83, 1.66) * mm, "end": v(-5.85, -2) * mm});
            skLineSegment(sketch, "E147", {"start": v(-8.2, 3.68) * mm, "end": v(-8.2, 0) * mm});
            skLineSegment(sketch, "E148.bottom", {"start": v(-11.5, -2) * mm, "end": v(-12, -2) * mm});
            skLineSegment(sketch, "E148.left", {"start": v(-11.5, -2) * mm, "end": v(-11.5, -0.77) * mm});
            skLineSegment(sketch, "E148.right", {"start": v(-12, -2) * mm, "end": v(-12, -0.77) * mm});
            skArc(sketch, "E149", {"start": v(-11.5, -0.77) * mm, "mid": v(-11.75, -0.52) * mm, "end": v(-12, -0.77) * mm});
            skLineSegment(sketch, "E150.1.0.0", {"start": v(-10.9, -2) * mm, "end": v(-10.9, -0.77) * mm});
            skLineSegment(sketch, "E150.1.0.1", {"start": v(-10.4, -2) * mm, "end": v(-10.4, -0.77) * mm});
            skArc(sketch, "E150.1.0.2", {"start": v(-10.4, -0.77) * mm, "mid": v(-10.65, -0.52) * mm, "end": v(-10.9, -0.77) * mm});
            skLineSegment(sketch, "E150.1.0.3", {"start": v(-10.4, -2) * mm, "end": v(-10.9, -2) * mm});
            skLineSegment(sketch, "E150.2.0.0", {"start": v(-9.8, -2) * mm, "end": v(-9.8, -0.77) * mm});
            skLineSegment(sketch, "E150.2.0.1", {"start": v(-9.3, -2) * mm, "end": v(-9.3, -0.77) * mm});
            skArc(sketch, "E150.2.0.2", {"start": v(-9.3, -0.77) * mm, "mid": v(-9.55, -0.52) * mm, "end": v(-9.8, -0.77) * mm});
            skLineSegment(sketch, "E150.2.0.3", {"start": v(-9.3, -2) * mm, "end": v(-9.8, -2) * mm});
            skLineSegment(sketch, "E150.direction1", {"start": v(-12, -2) * mm, "end": v(-10.9, -2) * mm, "construction": true});
            skLineSegment(sketch, "E151.trimOffspring", {"start": v(-8.2, 3.68) * mm, "end": v(-8.2, -5.96) * mm, "construction": true});
            skLineSegment(sketch, "E152", {"start": v(-2.83, 3.68) * mm, "end": v(-12.7, 3.68) * mm});
            skLineSegment(sketch, "E153", {"start": v(-12.7, 3.68) * mm, "end": v(-12.7, 2.94) * mm});
            skLineSegment(sketch, "E154", {"start": v(-11.75, -0.52) * mm, "end": v(-9.55, -0.52) * mm, "construction": true});
            skLineSegment(sketch, "E155.left", {"start": v(-3.89, 3.26) * mm, "end": v(-3.89, 1.94) * mm});
            skLineSegment(sketch, "E155.right", {"start": v(-3.33, 3.26) * mm, "end": v(-3.33, 1.94) * mm});
            skArc(sketch, "E156", {"start": v(-3.33, 3.26) * mm, "mid": v(-3.61, 3.53) * mm, "end": v(-3.89, 3.26) * mm});
            skArc(sketch, "E157", {"start": v(-3.89, 1.94) * mm, "mid": v(-3.61, 1.66) * mm, "end": v(-3.33, 1.94) * mm});
            skLineSegment(sketch, "E158", {"start": v(-2.83, 1.66) * mm, "end": v(-12.7, 1.66) * mm, "construction": true});
            skLineSegment(sketch, "E159", {"start": v(-2.83, 3.53) * mm, "end": v(-12.7, 3.53) * mm, "construction": true});
            skArc(sketch, "E160.1.0.0", {"start": v(-4.23, 3.26) * mm, "mid": v(-4.51, 3.53) * mm, "end": v(-4.79, 3.26) * mm});
            skLineSegment(sketch, "E160.1.0.1", {"start": v(-4.79, 3.26) * mm, "end": v(-4.79, 1.94) * mm});
            skLineSegment(sketch, "E160.1.0.2", {"start": v(-4.23, 3.26) * mm, "end": v(-4.23, 1.94) * mm});
            skArc(sketch, "E160.1.0.3", {"start": v(-4.79, 1.94) * mm, "mid": v(-4.51, 1.66) * mm, "end": v(-4.23, 1.94) * mm});
            skArc(sketch, "E160.2.0.0", {"start": v(-5.13, 3.26) * mm, "mid": v(-5.41, 3.53) * mm, "end": v(-5.69, 3.26) * mm});
            skLineSegment(sketch, "E160.2.0.1", {"start": v(-5.69, 3.26) * mm, "end": v(-5.69, 1.94) * mm});
            skLineSegment(sketch, "E160.2.0.2", {"start": v(-5.13, 3.26) * mm, "end": v(-5.13, 1.94) * mm});
            skArc(sketch, "E160.2.0.3", {"start": v(-5.69, 1.94) * mm, "mid": v(-5.41, 1.66) * mm, "end": v(-5.13, 1.94) * mm});
            skLineSegment(sketch, "E160.direction1", {"start": v(-3.89, 1.94) * mm, "end": v(-4.79, 1.94) * mm, "construction": true});
            skPoint(sketch, "E161.0", {"position": v(-4.2, 0) * mm});
            skPoint(sketch, "E162", {"position": v(-5.2, 3.68) * mm});
            skPoint(sketch, "E163", {"position": v(-4.2, 3.68) * mm});
            skSolve(sketch);
        }
        {
            var Q0;
            {var subQ10=sQuery(id+"F23.wireOp",EDGE,"E142");Q0=makeQuery(id+"F23.imprint","IMPRINT",FACE,{"disambiguationData":[TD([[makeQuery(id+"F23.imprint","IMPRINT",EDGE,{"derivedFrom":subQ10}),1.0]])]});}
            extrude(context, id + "F24", {"entities" : qUnion([Q0]), "operationType" : NewBodyOperationType.ADD, "oppositeDirection" : true, "depth" : 5.7 * mm, "offsetDistance" : 25 * mm});
        }
        {
            var Q0;
            Q0=makeQuery(id+"F24.opExtrude","SWEPT_FACE",FACE,{"disambiguationData":[OSD([sQuery(id+"F23.wireOp",EDGE,"E142")])]});
            var sketch = newSketch(context, id + "F25", { "sketchPlane" : qUnion([Q0])});
            skLineSegment(sketch, "E164.0", {"start": v(-5.7, 0) * mm, "end": v(-5.7, 0) * mm});
            skLineSegment(sketch, "E164.1", {"start": v(0, 0) * mm, "end": v(0, -2) * mm});
            skLineSegment(sketch, "E164.2", {"start": v(-3.7, -2) * mm, "end": v(0, -2) * mm});
            skPoint(sketch, "E165.visualSharp", {"position": v(-5.7, -2) * mm});
            skArc(sketch, "E165.filletArc", {"start": v(-5.7, 0) * mm, "mid": v(-5.11, -1.41) * mm, "end": v(-3.7, -2) * mm});
            skLineSegment(sketch, "E166.0", {"start": v(-2.85, 10.5) * mm, "end": v(-2.85, 0) * mm, "construction": true});
            skLineSegment(sketch, "E167", {"start": v(-2.85, 0) * mm, "end": v(-2.85, -2) * mm, "construction": true});
            skArc(sketch, "E168.0", {"start": v(-5.4, 0) * mm, "mid": v(-4.9, -1.2) * mm, "end": v(-3.7, -1.7) * mm});
            skArc(sketch, "E169.MirrorCS", {"start": v(-0.3, 0) * mm, "mid": v(-0.8, -1.2) * mm, "end": v(-2, -1.7) * mm});
            skArc(sketch, "E170.MirrorCS", {"start": v(0, 0) * mm, "mid": v(-0.59, -1.41) * mm, "end": v(-2, -2) * mm});
            skLineSegment(sketch, "E171", {"start": v(-3.7, -1.7) * mm, "end": v(-2, -1.7) * mm});
            skLineSegment(sketch, "E172", {"start": v(-2, -2) * mm, "end": v(-3.7, -2) * mm});
            skSolve(sketch);
        }
        {
            var Q0;
            {var subQ1=sQuery(id+"F23.wireOp",EDGE,"E142");var subQ2=makeQuery(id+"F24.opExtrude","CAP_EDGE",EDGE,{"disambiguationData":[OSD([subQ1])],"isStart":false});Q0=makeQuery(id+"F25.imprint","IMPRINT",FACE,{"disambiguationData":[TD([[makeQuery(id+"F25.imprint","IMPRINT",EDGE,{"derivedFrom":subQ2}),1.0]])]});}
            var Q1;
            {var subQ0=sQuery(id+"F25.wireOp",EDGE,"E164.1");Q1=makeQuery(id+"F25.imprint","IMPRINT",FACE,{"disambiguationData":[TD([[makeQuery(id+"F25.imprint","IMPRINT",EDGE,{"derivedFrom":subQ0}),-1.0]])]});}
            extrude(context, id + "F26", {"entities" : qUnion([Q0, Q1]), "operationType" : NewBodyOperationType.REMOVE, "oppositeDirection" : true, "depth" : 8.5 * mm, "offsetDistance" : 25 * mm});
        }
        {
            var Q0;
            {var subQ0=sQuery(id+"F25.wireOp",EDGE,"E171");Q0=makeQuery(id+"F25.imprint","IMPRINT",FACE,{"disambiguationData":[TD([[makeQuery(id+"F25.imprint","IMPRINT",EDGE,{"derivedFrom":subQ0}),1.0]])]});}
            var Q1;
            Q1=sQuery(id+"F25.wireOp",EDGE,"E168.0");
            var Q2;
            Q2=sQuery(id+"F25.wireOp",EDGE,"E171");
            var Q3;
            Q3=sQuery(id+"F25.wireOp",EDGE,"E169.MirrorCS");
            extrude(context, id + "F27", {"entities" : qUnion([Q0]), "operationType" : NewBodyOperationType.ADD, "surfaceEntities" : qUnion([Q1, Q2, Q3]), "oppositeDirection" : true, "depth" : 6 * mm, "offsetDistance" : 25 * mm});
        }
        {
            var Q0;
            Q0=makeQuery(id+"F23.imprint","IMPRINT",FACE,{"disambiguationData":[TD([[makeQuery(id+"F23.imprint","IMPRINT",EDGE,{"derivedFrom":sQuery(id+"F23.wireOp",EDGE,"E160.1.0.0")}),1.0]])]});
            var Q1;
            {var subQ1=sQuery(id+"F23.wireOp",EDGE,"E160.2.0.1");Q1=makeQuery(id+"F23.imprint","IMPRINT",FACE,{"disambiguationData":[TD([[makeQuery(id+"F23.imprint","IMPRINT",EDGE,{"derivedFrom":subQ1}),1.0]])]});}
            var Q2;
            Q2=makeQuery(id+"F23.imprint","IMPRINT",FACE,{"disambiguationData":[TD([[makeQuery(id+"F23.imprint","IMPRINT",EDGE,{"derivedFrom":sQuery(id+"F23.wireOp",EDGE,"E155.left")}),1.0]])]});
            extrude(context, id + "F28", {"entities" : qUnion([Q0, Q1, Q2]), "operationType" : NewBodyOperationType.REMOVE, "oppositeDirection" : true, "depth" : 25 * mm, "offsetDistance" : 25 * mm});
        }
        {
            var Q0;
            {var subQ6=sQuery(id+"F23.wireOp",EDGE,"E145");Q0=makeQuery(id+"F24.boolean.opBoolean","SPLIT",FACE,{"disambiguationData":[TD([makeQuery(id+"F6.opExtrude","SWEPT_FACE",FACE,{"disambiguationData":[OSD([sQuery(id+"F5.wireOp",EDGE,"E19.2")])]})])],"derivedFrom":makeQuery(id+"F24.opExtrude","SWEPT_FACE",FACE,{"disambiguationData":[OSD([subQ6])]})});}
            var sketch = newSketch(context, id + "F29", { "sketchPlane" : qUnion([Q0])});
            skLineSegment(sketch, "E173.0", {"start": v(0, 3.68) * mm, "end": v(0, 1.66) * mm});
            skLineSegment(sketch, "E174.0", {"start": v(0.3, 3.68) * mm, "end": v(0.3, 1.66) * mm});
            skLineSegment(sketch, "E175.MirrorCS", {"start": v(5.4, 3.68) * mm, "end": v(5.4, 1.66) * mm});
            skLineSegment(sketch, "E176.0", {"start": v(5.4, 1.66) * mm, "end": v(4.27, 1.66) * mm});
            skLineSegment(sketch, "E177.0", {"start": v(5.4, 3.68) * mm, "end": v(4.5, 3.68) * mm});
            skPoint(sketch, "E178.0.start.orphan", {"position": v(5.7, 3.68) * mm});
            skPoint(sketch, "E179.orphan", {"position": v(5.7, 1.66) * mm});
            skLineSegment(sketch, "E180", {"start": v(0.3, 3.68) * mm, "end": v(1.1, 3.68) * mm});
            skLineSegment(sketch, "E181", {"start": v(1.1, 3.68) * mm, "end": v(1.1, 1.66) * mm});
            skLineSegment(sketch, "E182", {"start": v(0.3, 1.66) * mm, "end": v(1.1, 1.66) * mm});
            skLineSegment(sketch, "E183", {"start": v(4.5, 3.68) * mm, "end": v(4.27, 1.66) * mm});
            skSolve(sketch);
        }
        {
            var Q0;
            {var subQ0=sQuery(id+"F29.wireOp",EDGE,"E174.0");Q0=makeQuery(id+"F29.imprint","IMPRINT",FACE,{"disambiguationData":[TD([[makeQuery(id+"F29.imprint","IMPRINT",EDGE,{"derivedFrom":subQ0}),1.0]])]});}
            var Q1;
            Q1=makeQuery(id+"F29.imprint","IMPRINT",FACE,{"disambiguationData":[TD([[makeQuery(id+"F29.imprint","IMPRINT",EDGE,{"derivedFrom":sQuery(id+"F29.wireOp",EDGE,"E176.0")}),-1.0]])]});
            extrude(context, id + "F30", {"entities" : qUnion([Q0, Q1]), "operationType" : NewBodyOperationType.ADD, "oppositeDirection" : true, "depth" : 5 * mm, "offsetDistance" : 25 * mm});
        }
    });
